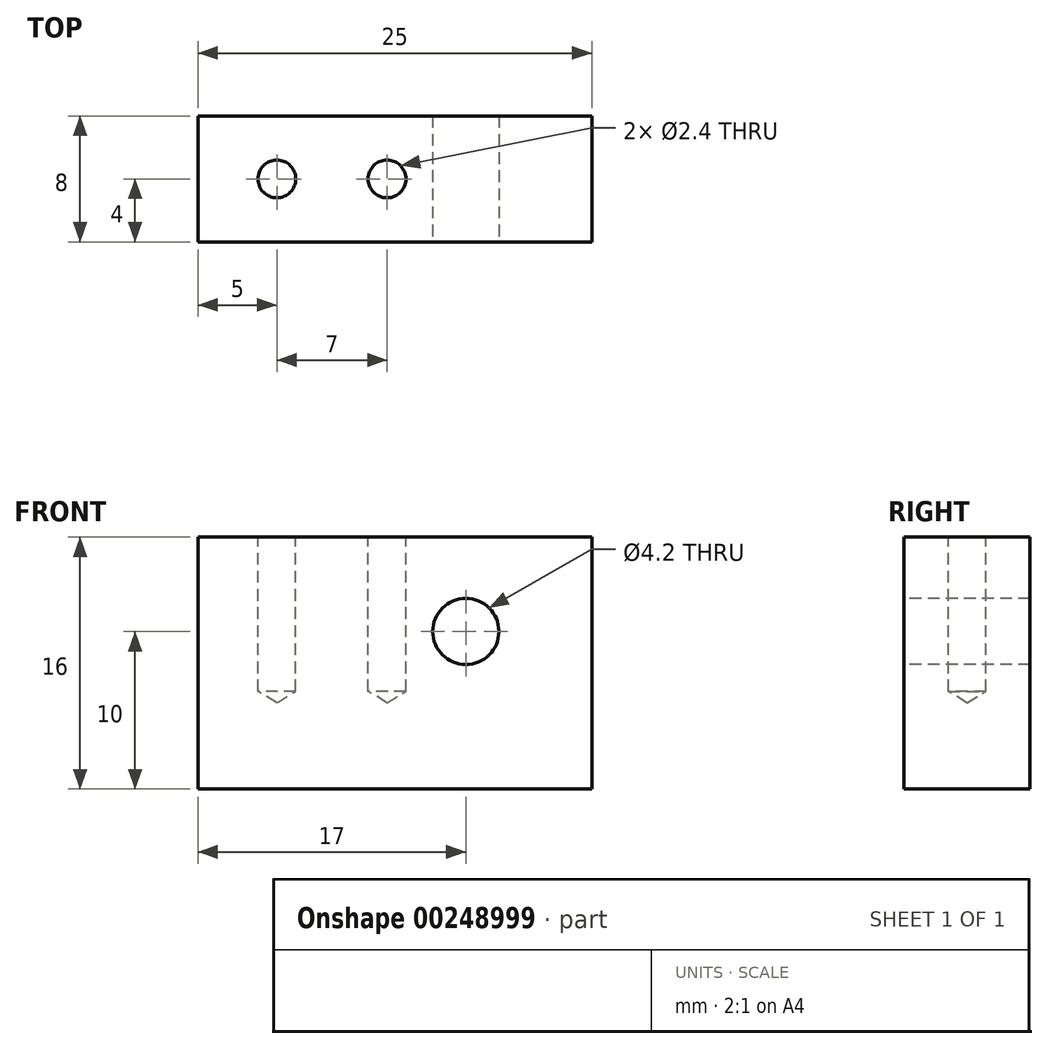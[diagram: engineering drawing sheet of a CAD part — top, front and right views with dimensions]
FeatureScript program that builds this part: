
annotation { "Feature Type Name" : "Feature", "Feature Type Description" : "" }
export const myFeature = defineFeature(function(context is Context, id is Id, definition is map)
    precondition{}
    {
        {
            var Q0;
            Q0=qCreatedBy(makeId("Front.planeOp"),FACE);
            var sketch = newSketch(context, id + "F0", { "sketchPlane" : qUnion([Q0])});
            skLineSegment(sketch, "E0.bottom", {"start": v(12.5, 8) * mm, "end": v(-12.5, 8) * mm});
            skLineSegment(sketch, "E0.top", {"start": v(12.5, -8) * mm, "end": v(-12.5, -8) * mm});
            skLineSegment(sketch, "E0.left", {"start": v(12.5, 8) * mm, "end": v(12.5, -8) * mm});
            skLineSegment(sketch, "E0.right", {"start": v(-12.5, 8) * mm, "end": v(-12.5, -8) * mm});
            skPoint(sketch, "E0.middle", {"position": v(0, 0) * mm});
            skSolve(sketch);
        }
        {
            var Q0;
            Q0=makeQuery(id+"F0.imprint","IMPRINT",FACE,{"disambiguationData":[TD([[makeQuery(id+"F0.imprint","IMPRINT",EDGE,{"derivedFrom":sQuery(id+"F0.wireOp",EDGE,"E0.bottom")}),1.0]])]});
            extrude(context, id + "F1", {"entities" : qUnion([Q0]), "endBound" : BoundingType.SYMMETRIC, "depth" : 8 * mm});
        }
        {
            var Q0;
            Q0=makeQuery(id+"F1.opExtrude","CAP_FACE",FACE,{"disambiguationData":[OSD([sQuery(id+"F0.wireOp",EDGE,"E0.bottom"),sQuery(id+"F0.wireOp",EDGE,"E0.top"),sQuery(id+"F0.wireOp",EDGE,"E0.left"),sQuery(id+"F0.wireOp",EDGE,"E0.right")])],"isStart":false});
            var sketch = newSketch(context, id + "F2", { "sketchPlane" : qUnion([Q0])});
            skPoint(sketch, "E1", {"position": v(4.5, 2) * mm});
            skSolve(sketch);
        }
        {
            var Q0;
            Q0=sQuery(id+"F2.wireOp",VERTEX,"E1");
            var Q1;
            Q1=makeQuery(id+"F1.opExtrude","SWEPT_BODY",BODY,{"disambiguationData":[OSD([sQuery(id+"F0.wireOp",EDGE,"E0.bottom"),sQuery(id+"F0.wireOp",EDGE,"E0.top"),sQuery(id+"F0.wireOp",EDGE,"E0.left"),sQuery(id+"F0.wireOp",EDGE,"E0.right")])]});
            hole(context, id + "F3", {"style" : HoleStyle.SIMPLE, "endStyle" : HoleEndStyle.BLIND, "standardTappedOrClearance" : lookupTablePath({ "standard" : "ISO", "engagement" : "75%", "pitch" : "0.8 mm", "size" : "M5", "type" : "Tapped" }), "standardBlindInLast" : lookupTablePath({ "standard" : "ISO", "engagement" : "75%", "pitch" : "0.8 mm", "size" : "M5", "type" : "Tapped" }), "holeDiameter" : 4.2 * mm, "showTappedDepth" : true, "holeDepth" : 14.4 * mm, "tappedDepth" : 12 * mm, "tapClearance" : 3, "startFromSketch" : true, "locations" : qUnion([Q0]), "scope" : qUnion([Q1]), "majorDiameter" : 5 * mm});
        }
        {
            var Q0;
            Q0=makeQuery(id+"F1.opExtrude","SWEPT_FACE",FACE,{"disambiguationData":[OSD([sQuery(id+"F0.wireOp",EDGE,"E0.bottom")])]});
            var sketch = newSketch(context, id + "F4", { "sketchPlane" : qUnion([Q0])});
            skPoint(sketch, "E2", {"position": v(-7.5, 0) * mm});
            skPoint(sketch, "E3", {"position": v(-0.5, 0) * mm});
            skSolve(sketch);
        }
        {
            var Q0;
            Q0=sQuery(id+"F4.wireOp",VERTEX,"E3");
            var Q1;
            Q1=sQuery(id+"F4.wireOp",VERTEX,"E2");
            var Q2;
            Q2=makeQuery(id+"F1.opExtrude","SWEPT_BODY",BODY,{"disambiguationData":[OSD([sQuery(id+"F0.wireOp",EDGE,"E0.bottom"),sQuery(id+"F0.wireOp",EDGE,"E0.top"),sQuery(id+"F0.wireOp",EDGE,"E0.left"),sQuery(id+"F0.wireOp",EDGE,"E0.right")])]});
            hole(context, id + "F5", {"style" : HoleStyle.SIMPLE, "endStyle" : HoleEndStyle.BLIND, "standardTappedOrClearance" : lookupTablePath({ "standard" : "ISO", "engagement" : "75%", "pitch" : "0.6 mm", "size" : "M3", "type" : "Tapped" }), "standardBlindInLast" : lookupTablePath({ "standard" : "ISO", "engagement" : "75%", "pitch" : "0.6 mm", "size" : "M3", "type" : "Tapped" }), "holeDiameter" : 2.4 * mm, "showTappedDepth" : true, "holeDepth" : 9.8 * mm, "tappedDepth" : 8 * mm, "tapClearance" : 3, "startFromSketch" : true, "locations" : qUnion([Q0, Q1]), "scope" : qUnion([Q2])});
        }
    });
